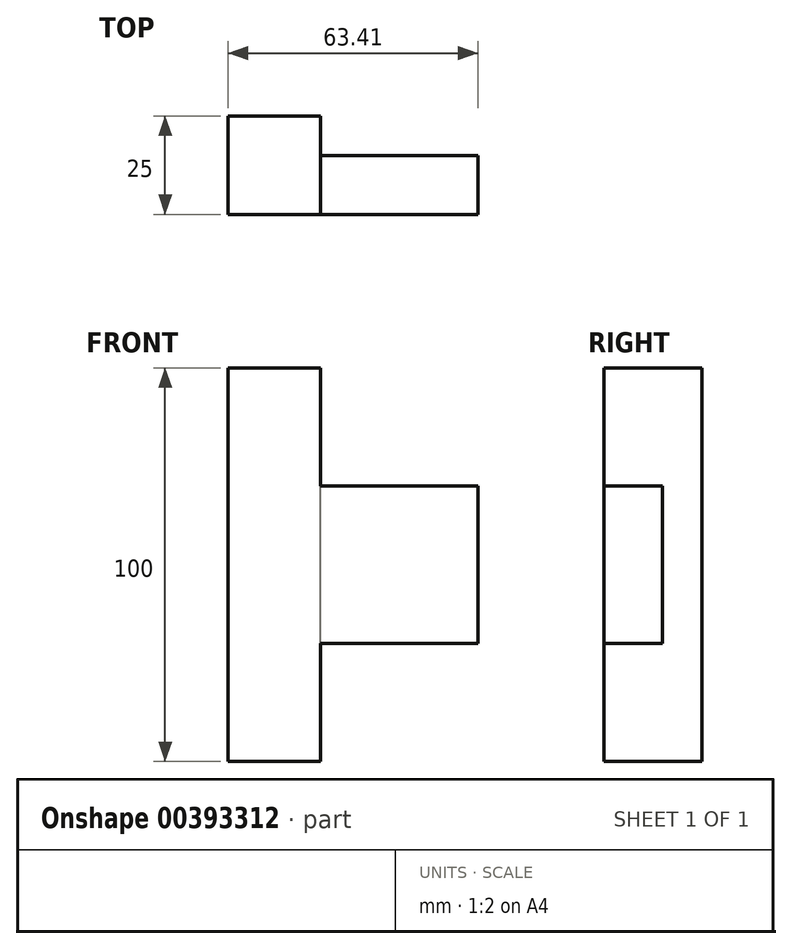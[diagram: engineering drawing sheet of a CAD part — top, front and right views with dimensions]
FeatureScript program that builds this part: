
annotation { "Feature Type Name" : "Feature", "Feature Type Description" : "" }
export const myFeature = defineFeature(function(context is Context, id is Id, definition is map)
    precondition{}
    {
        {
            var Q0;
            Q0=qCreatedBy(makeId("Front.planeOp"),FACE);
            var sketch = newSketch(context, id + "F0", { "sketchPlane" : qUnion([Q0])});
            skLineSegment(sketch, "E0.bottom", {"start": v(0, 0) * mm, "end": v(23.41, 0) * mm});
            skLineSegment(sketch, "E0.top", {"start": v(0, 100) * mm, "end": v(23.41, 100) * mm});
            skLineSegment(sketch, "E0.left", {"start": v(0, 0) * mm, "end": v(0, 100) * mm});
            skLineSegment(sketch, "E0.right", {"start": v(23.41, 0) * mm, "end": v(23.41, 100) * mm});
            skSolve(sketch);
        }
        {
            var Q0;
            Q0=makeQuery(id+"F0.imprint","IMPRINT",FACE,{"disambiguationData":[TD([[makeQuery(id+"F0.imprint","IMPRINT",EDGE,{"derivedFrom":sQuery(id+"F0.wireOp",EDGE,"E0.bottom")}),1.0]])]});
            extrude(context, id + "F1", {"entities" : qUnion([Q0]), "depth" : 25 * mm});
        }
        {
            var Q0;
            Q0=makeQuery(id+"F1.opExtrude","SWEPT_FACE",FACE,{"disambiguationData":[OSD([sQuery(id+"F0.wireOp",EDGE,"E0.right")])]});
            var sketch = newSketch(context, id + "F2", { "sketchPlane" : qUnion([Q0])});
            skLineSegment(sketch, "E1.bottom", {"start": v(-25, 50) * mm, "end": v(-10.1, 50) * mm});
            skLineSegment(sketch, "E1.top", {"start": v(-25, 30) * mm, "end": v(-10.1, 30) * mm});
            skLineSegment(sketch, "E1.left", {"start": v(-25, 50) * mm, "end": v(-25, 30) * mm});
            skLineSegment(sketch, "E1.right", {"start": v(-10.1, 50) * mm, "end": v(-10.1, 30) * mm});
            skLineSegment(sketch, "E2.top", {"start": v(-25, 70) * mm, "end": v(-10.1, 70) * mm});
            skLineSegment(sketch, "E2.left", {"start": v(-25, 50) * mm, "end": v(-25, 70) * mm});
            skLineSegment(sketch, "E2.right", {"start": v(-10.1, 50) * mm, "end": v(-10.1, 70) * mm});
            skSolve(sketch);
        }
        {
            var Q0;
            Q0=makeQuery(id+"F2.imprint","IMPRINT",FACE,{"disambiguationData":[TD([[makeQuery(id+"F2.imprint","IMPRINT",EDGE,{"derivedFrom":sQuery(id+"F2.wireOp",EDGE,"E1.bottom")}),1.0]])]});
            var Q1;
            Q1=makeQuery(id+"F2.imprint","IMPRINT",FACE,{"disambiguationData":[TD([[makeQuery(id+"F2.imprint","IMPRINT",EDGE,{"derivedFrom":sQuery(id+"F2.wireOp",EDGE,"E1.top")}),1.0]])]});
            extrude(context, id + "F3", {"entities" : qUnion([Q0, Q1]), "operationType" : NewBodyOperationType.ADD, "depth" : 40 * mm});
        }
    });
